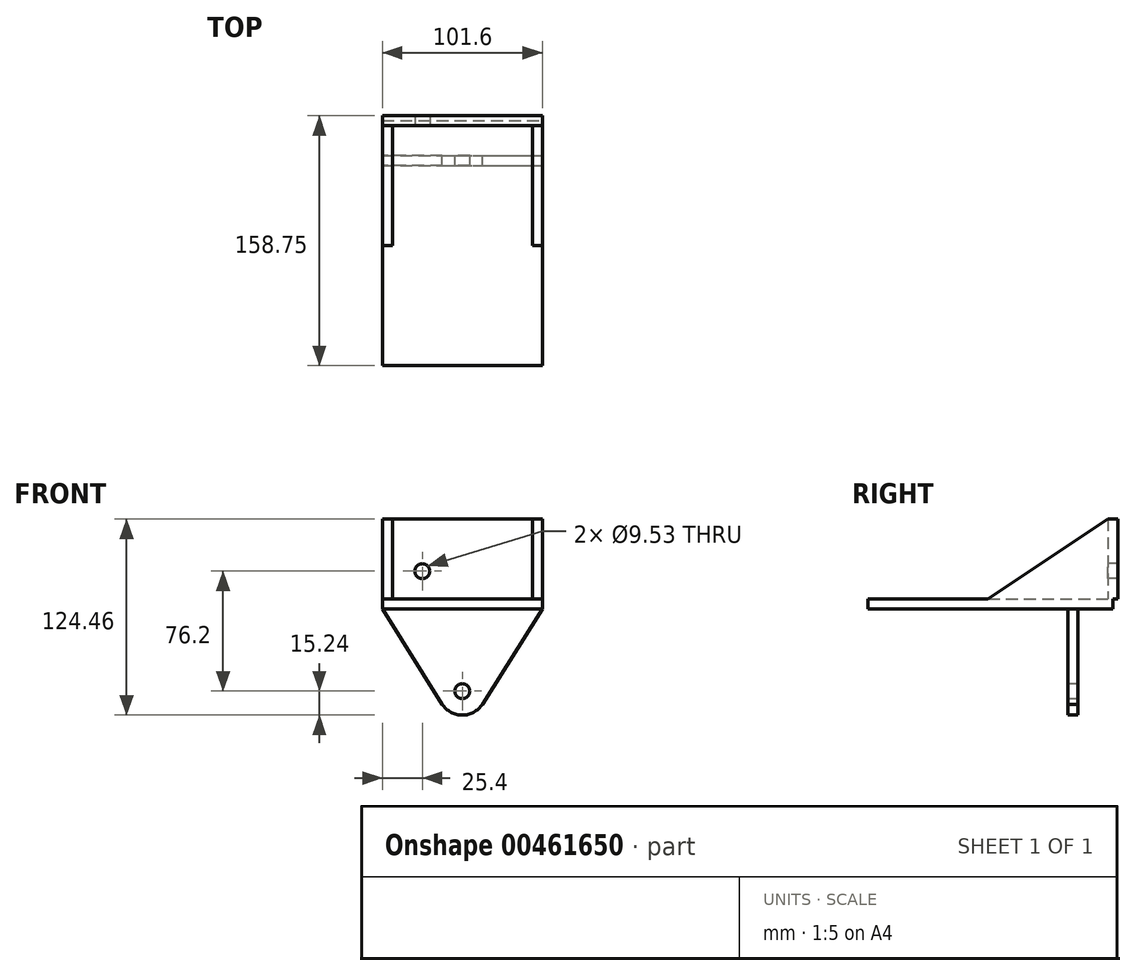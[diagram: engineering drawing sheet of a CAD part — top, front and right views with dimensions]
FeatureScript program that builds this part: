
annotation { "Feature Type Name" : "Feature", "Feature Type Description" : "" }
export const myFeature = defineFeature(function(context is Context, id is Id, definition is map)
    precondition{}
    {
        {
            var Q0;
            Q0=qCreatedBy(makeId("Front.planeOp"),FACE);
            var sketch = newSketch(context, id + "F0", { "sketchPlane" : qUnion([Q0])});
            skLineSegment(sketch, "E0.bottom", {"start": v(50.8, 25.4) * mm, "end": v(-50.8, 25.4) * mm});
            skLineSegment(sketch, "E0.top", {"start": v(50.8, -25.4) * mm, "end": v(-50.8, -25.4) * mm});
            skLineSegment(sketch, "E0.left", {"start": v(50.8, 25.4) * mm, "end": v(50.8, -25.4) * mm});
            skLineSegment(sketch, "E0.right", {"start": v(-50.8, 25.4) * mm, "end": v(-50.8, -25.4) * mm});
            skPoint(sketch, "E0.middle", {"position": v(0, 0) * mm});
            skSolve(sketch);
        }
        {
            var Q0;
            Q0=makeQuery(id+"F0.imprint","IMPRINT",FACE,{"disambiguationData":[TD([[makeQuery(id+"F0.imprint","IMPRINT",EDGE,{"derivedFrom":sQuery(id+"F0.wireOp",EDGE,"E0.bottom")}),1.0]])]});
            extrude(context, id + "F1", {"entities" : qUnion([Q0]), "depth" : 6.35 * mm});
        }
        {
            var Q0;
            Q0=makeQuery(id+"F1.opExtrude","CAP_FACE",FACE,{"disambiguationData":[OSD([sQuery(id+"F0.wireOp",EDGE,"E0.bottom"),sQuery(id+"F0.wireOp",EDGE,"E0.top"),sQuery(id+"F0.wireOp",EDGE,"E0.left"),sQuery(id+"F0.wireOp",EDGE,"E0.right")])],"isStart":false});
            var sketch = newSketch(context, id + "F2", { "sketchPlane" : qUnion([Q0])});
            skLineSegment(sketch, "E1.bottom", {"start": v(-50.8, -25.4) * mm, "end": v(50.8, -25.4) * mm});
            skLineSegment(sketch, "E1.top", {"start": v(-50.8, -31.75) * mm, "end": v(50.8, -31.75) * mm});
            skLineSegment(sketch, "E1.left", {"start": v(-50.8, -25.4) * mm, "end": v(-50.8, -31.75) * mm});
            skLineSegment(sketch, "E1.right", {"start": v(50.8, -25.4) * mm, "end": v(50.8, -31.75) * mm});
            skSolve(sketch);
        }
        {
            var Q0;
            Q0=makeQuery(id+"F2.imprint","IMPRINT",FACE,{"disambiguationData":[TD([[makeQuery(id+"F2.imprint","IMPRINT",EDGE,{"derivedFrom":sQuery(id+"F2.wireOp",EDGE,"E1.bottom")}),1.0]])]});
            extrude(context, id + "F3", {"entities" : qUnion([Q0]), "operationType" : NewBodyOperationType.ADD, "depth" : 152.4 * mm, "hasSecondDirection" : true, "secondDirectionOppositeDirection" : true, "secondDirectionDepth" : 3.17 * mm});
        }
        {
            var Q0;
            Q0=makeQuery(id+"F3.boolean.opBoolean","MERGE",FACE,{"derivedFrom":[makeQuery(id+"F1.opExtrude","SWEPT_FACE",FACE,{"disambiguationData":[OSD([sQuery(id+"F0.wireOp",EDGE,"E0.left")])]}),makeQuery(id+"F3.opExtrude","SWEPT_FACE",FACE,{"disambiguationData":[OSD([sQuery(id+"F2.wireOp",EDGE,"E1.right")])]})]});
            var sketch = newSketch(context, id + "F4", { "sketchPlane" : qUnion([Q0])});
            skLineSegment(sketch, "E2", {"start": v(-6.35, -25.4) * mm, "end": v(-6.35, 25.4) * mm});
            skLineSegment(sketch, "E3", {"start": v(-6.35, 25.4) * mm, "end": v(-82.55, -25.4) * mm});
            skLineSegment(sketch, "E4", {"start": v(-82.55, -25.4) * mm, "end": v(-6.35, -25.4) * mm});
            skSolve(sketch);
        }
        {
            var Q0;
            Q0=makeQuery(id+"F3.boolean.opBoolean","MERGE",FACE,{"derivedFrom":[makeQuery(id+"F1.opExtrude","SWEPT_FACE",FACE,{"disambiguationData":[OSD([sQuery(id+"F0.wireOp",EDGE,"E0.right")])]}),makeQuery(id+"F3.opExtrude","SWEPT_FACE",FACE,{"disambiguationData":[OSD([sQuery(id+"F2.wireOp",EDGE,"E1.left")])]})]});
            var sketch = newSketch(context, id + "F5", { "sketchPlane" : qUnion([Q0])});
            skLineSegment(sketch, "E5", {"start": v(6.35, 25.4) * mm, "end": v(82.55, -25.4) * mm});
            skLineSegment(sketch, "E6", {"start": v(82.55, -25.4) * mm, "end": v(6.35, -25.4) * mm});
            skLineSegment(sketch, "E7", {"start": v(6.35, -25.4) * mm, "end": v(6.35, 25.4) * mm});
            skSolve(sketch);
        }
        {
            var Q0;
            Q0=qCreatedBy(makeId("Front.planeOp"),FACE);
            cPlane(context, id + "F6", {"entities" : qUnion([Q0]), "cplaneType" : CPlaneType.OFFSET, "offset" : 25.4 * mm, "width" : 152.4 * mm, "height" : 152.4 * mm});
        }
        {
            var Q0;
            Q0=makeQuery(id+"F1.opExtrude","CAP_FACE",FACE,{"disambiguationData":[OSD([sQuery(id+"F0.wireOp",EDGE,"E0.bottom"),sQuery(id+"F0.wireOp",EDGE,"E0.top"),sQuery(id+"F0.wireOp",EDGE,"E0.left"),sQuery(id+"F0.wireOp",EDGE,"E0.right")])],"isStart":false});
            var sketch = newSketch(context, id + "F7", { "sketchPlane" : qUnion([Q0])});
            skCircle(sketch, "E8", {"center": v(-25.4, -7.62) * mm, "radius": 4.76 * mm});
            skSolve(sketch);
        }
        {
            var Q0;
            Q0=qCreatedBy(id+"F6.planeOp",FACE);
            var sketch = newSketch(context, id + "F8", { "sketchPlane" : qUnion([Q0])});
            skArc(sketch, "E9", {"start": v(-13, -91.76) * mm, "mid": v(0, -99.06) * mm, "end": v(13, -91.76) * mm});
            skLineSegment(sketch, "E10.0", {"start": v(-50.8, -31.75) * mm, "end": v(50.8, -31.75) * mm});
            skLineSegment(sketch, "E11", {"start": v(-12.78, -92.12) * mm, "end": v(-50.8, -31.75) * mm});
            skLineSegment(sketch, "E12", {"start": v(12.78, -92.12) * mm, "end": v(50.8, -31.75) * mm});
            skCircle(sketch, "E13", {"center": v(0, -83.82) * mm, "radius": 4.76 * mm});
            skSolve(sketch);
        }
        {
            var Q0;
            {var subQ3=sQuery(id+"F8.wireOp",EDGE,"E10.0");Q0=makeQuery(id+"F8.imprint","IMPRINT",FACE,{"disambiguationData":[TD([[makeQuery(id+"F8.imprint","IMPRINT",EDGE,{"derivedFrom":subQ3}),-1.0]])]});}
            extrude(context, id + "F9", {"entities" : qUnion([Q0]), "operationType" : NewBodyOperationType.ADD, "depth" : 6.35 * mm});
        }
        {
            var Q0;
            Q0=makeQuery(id+"F5.imprint","IMPRINT",FACE,{"disambiguationData":[TD([[makeQuery(id+"F5.imprint","IMPRINT",EDGE,{"derivedFrom":sQuery(id+"F5.wireOp",EDGE,"E5")}),-1.0]])]});
            extrude(context, id + "F10", {"entities" : qUnion([Q0]), "operationType" : NewBodyOperationType.ADD, "oppositeDirection" : true, "depth" : 6.35 * mm});
        }
        {
            var Q0;
            Q0=makeQuery(id+"F4.imprint","IMPRINT",FACE,{"disambiguationData":[TD([[makeQuery(id+"F4.imprint","IMPRINT",EDGE,{"derivedFrom":sQuery(id+"F4.wireOp",EDGE,"E2")}),-1.0]])]});
            extrude(context, id + "F11", {"entities" : qUnion([Q0]), "operationType" : NewBodyOperationType.ADD, "oppositeDirection" : true, "depth" : 6.35 * mm});
        }
        {
            var Q0;
            Q0=sQuery(id+"F7.wireOp",VERTEX,"E8.center");
            var Q1;
            Q1=makeQuery(id+"F1.opExtrude","SWEPT_BODY",BODY,{"disambiguationData":[OSD([sQuery(id+"F0.wireOp",EDGE,"E0.bottom"),sQuery(id+"F0.wireOp",EDGE,"E0.top"),sQuery(id+"F0.wireOp",EDGE,"E0.left"),sQuery(id+"F0.wireOp",EDGE,"E0.right")])]});
            hole(context, id + "F12", {"style" : HoleStyle.SIMPLE, "endStyle" : HoleEndStyle.THROUGH, "holeDiameter" : 9.52 * mm, "isTappedThrough" : true, "tappedDepth" : 12.7 * mm, "tapClearance" : 3, "locations" : qUnion([Q0]), "scope" : qUnion([Q1])});
        }
    });
